# Revit family: Wicslide_160_6_leaf_3_track_sliding_2_outer_ends_fixed_4_inner_leafs_slide
name_source: partatom
category: Doors
revit_build: Autodesk Revit Architecture 2014 (Build: 20130308_1515(x64)
units: mm (PartAtom-declared; Revit-internal decimal feet)

## types (1)
- Wicslide_160_6_leaf_3_track_sliding_2_outer_ends_fixed_4_inner_leafs_slide
    Acoustic = Rw (C;Cu)= 47 (-1;-4)dB
    Analytic Construction = <None>
    Assembly Code = B2030110
    Bottom Offset = 45 mm  [stored 0.147638 ft]
    Corrosion Resistance of the Fittings = Class 5
    Date of publishing = 3/14/2015
    Description = The new WICSLIDE 160 lifting sliding system combines excellent thermal insulation with highest functionality and design. Impressive leaf dimensions and enduring operation comfort are your guarantors for maximum customer satisfaction. With state-of-the-art technology and innovative advantages in fabrication WICSLIDE 160 is a high-tech product that sets new standards.
    Design country = Germany
    Door 1 width = 1245 mm
    Door 2 width = 2455 mm
    Door 3 width = 3762 mm
    Door 4 width = 4963 mm
    Door Offset = 123 mm
    EN1627 Burglar Resistance = RC1N, RC2N, RC2, RC3, SBD
    Edition number = 1
    Frame 1940019 = Yes
    Frame Depth = 245 mm  [stored 0.803806 ft]
    Frame Material = WICONA - Aluminium - RAL7016 - Anthracite Grey - Matt
    Frame Width = 67 mm
    Frame Width 2 = 52 mm
    Frame Width 3 = 43 mm
    Function = Interior
    Glass Material = WICONA -  Glass
    Glass Offset 1 = 138 mm
    Glass Offset 2 = 37 mm  [stored 0.121391 ft]
    Handle Material = Aluminium
    Height = 2100 mm  [stored 6.88976 ft]
    Keynote = L20/520
    Leaf Height All = 1996 mm
    Leaf Material = WICONA - Aluminium - RAL7016 - Anthracite Grey - Matt
    Leaf Width all = 1283 mm
    Load Bearing Capacity of Safety Devices = Fulfilled
    Manufacturer = Wicona
    Manufacturer country = Germany
    Manufacturer name = Wicona
    Material main = Aluminium
    Material secondary = Glass
    Maximum Sash Weight = 160kg as standard design, heavier weights can easily be customised
    Mechanical Strength = Class 4
    Model = Wicslide 160
    Nominal height = 341300
    Nominal width = 323500
    Operating Forces = Class 1
    Operation = IFC_DOORSLIDING
    Product Guid = 0afd48ae-a14c-4f29-91d5-9573b3650314
    Product SKU = WICSLIDE_160_W
    Product data url = http://bimobject.com
    Product family = Windows & Doors
    Product group = Windows
    QR code = http://bimobject.com
    Quality Assurance = Certified according to ISO 9001:2008
    Repeated Opening/Closing = Class 3 (20,000 Cycles)
    Resistance to wind load = Class C3
    Type Comments = Stand Alone
    URL = http://www.wicona.com
    Uniclass2 = Ss-25-30-20-77
    Vent Frame 1940037 & 1040010 = Yes
    Vent Frame 1940037 & 1940041 = No
    Wall Closure = By host
    Watertightness = E1350A
    Weight Net (Kg) = 0
    Width = 7500 mm  [stored 24.6063 ft]

note: [stored X ft] marks values corroborated as IEEE doubles in the binary element streams (Revit-internal decimal feet)

## geometry (parser evidence)
native form markers: Blend x4, Sweep x38
no freeform markers — native parametric forms only
